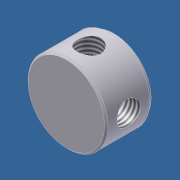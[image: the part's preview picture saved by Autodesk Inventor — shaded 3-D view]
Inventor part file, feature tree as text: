
AUTODESK INVENTOR PART (.ipt)
format: ipt  version: 2011 (Build 150239000, 239)  size: 125,952 bytes
history: native  units: in
note: dims shown in document units (in); Inventor stores cm internally (conversion verified against a paired STEP export)
features: sketch x5, extrude x4, thread x4, plane x3, chamfer x1, projected_geometry x1
ambient origin geometry x8: Origin, YZ Plane, XZ Plane, XY Plane, X Axis, Y Axis, Z Axis, Center Point
bodies: Solid1 (feature_tree)
feature tree (18):
  extrude  "Extrusion1"  Depth=0.775in TaperAngle=0.0deg
  chamfer  "Chamfer1"  Distance=0.0312in Angle=45.0deg
  extrude  "Extrusion2"  Depth=0.075in TaperAngle=0.0deg
  plane  "Work Plane1"
  extrude  "Extrusion3"  Depth=0.425in
  plane  "Work Plane2"
  sketch  "Sketch4"  dims[d11=3.0in d12=0.0in d13=0.0in d14=0.0in d15=0.425in d16=3.0in d17=0.0in d18=1.0in d19=0.0in]
  plane  "Work Plane3"
  extrude  "Extrusion4"  TaperAngle=0.0deg  [1 undecoded]
  thread  "Thread1"  [1 undecoded]
  thread  "Thread2"  [1 undecoded]
  thread  "Thread3"  [1 undecoded]
  thread  "Thread4"  [1 undecoded]
  sketch  "Sketch1"  dims[d0=1.425in d1=0.775in d2=0.0in d3=0.0312in d4=0.125in d5=45.0deg]
  sketch  "Sketch2"  dims[d6=1.325in d7=0.075in d8=0.0in]
  sketch  "Sketch3"  dims[d9=0.0in d10=0.425in]
  projected_geometry  "Projected Loop1"
  sketch  "Sketch5"  dims[d20=1.0in d21=0.0in d22=1.0in d23=0.0in d24=1.0in d25=0.0in]
note: 5 required parameter values undecoded (feature->parameter linkage not recoverable at this tier; creation-order binding heuristic only, values carry confidence <= 0.55)
